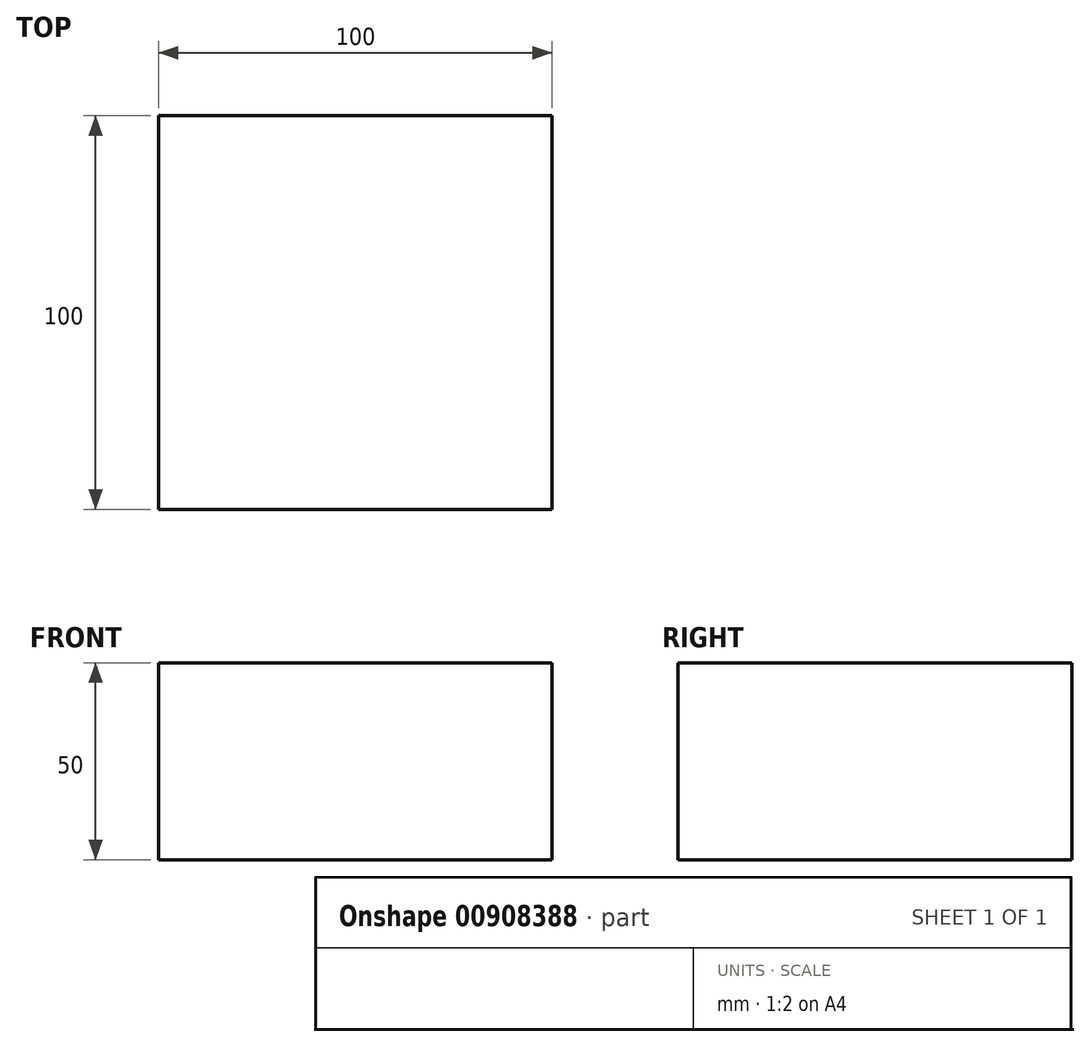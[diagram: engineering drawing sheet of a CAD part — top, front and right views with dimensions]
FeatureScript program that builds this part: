
annotation { "Feature Type Name" : "Feature", "Feature Type Description" : "" }
export const myFeature = defineFeature(function(context is Context, id is Id, definition is map)
    precondition{}
    {
        {
            var Q0;
            Q0=qCreatedBy(makeId("Front.planeOp"),FACE);
            var sketch = newSketch(context, id + "F0", { "sketchPlane" : qUnion([Q0])});
            skPoint(sketch, "E0.0", {"position": v(0, 0) * mm});
            skLineSegment(sketch, "E1.bottom", {"start": v(0, 0) * mm, "end": v(100, 0) * mm});
            skLineSegment(sketch, "E1.top", {"start": v(0, -50) * mm, "end": v(100, -50) * mm});
            skLineSegment(sketch, "E1.left", {"start": v(0, 0) * mm, "end": v(0, -50) * mm});
            skLineSegment(sketch, "E1.right", {"start": v(100, 0) * mm, "end": v(100, -50) * mm});
            skSolve(sketch);
        }
        {
            var Q0;
            Q0=makeQuery(id+"F0.imprint","IMPRINT",FACE,{"disambiguationData":[TD([[makeQuery(id+"F0.imprint","IMPRINT",EDGE,{"derivedFrom":sQuery(id+"F0.wireOp",EDGE,"E1.bottom")}),-1.0]])]});
            extrude(context, id + "F1", {"entities" : qUnion([Q0]), "depth" : 100 * mm, "offsetDistance" : 25 * mm});
        }
    });
